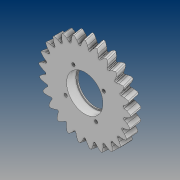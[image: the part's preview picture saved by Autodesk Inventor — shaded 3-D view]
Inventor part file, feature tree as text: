
AUTODESK INVENTOR PART (.ipt)
format: ipt  version: 2021 (Build 250183000, 183)  size: 912,896 bytes
history: native  units: in
note: dims shown in document units (in); Inventor stores cm internally (conversion verified against a paired STEP export)
features: thread x4, sketch x4, extrude x3, pattern_circular x2, plane x1, revolve x1
ambient origin geometry x8: Origin, YZ Plane, XZ Plane, XY Plane, X Axis, Y Axis, Z Axis, Center Point
bodies: Solid2 (feature_tree), Solid1 (feature_tree)
feature tree (15):
  extrude  "Extrusion1"  Depth=0.9055in TaperAngle=0.0deg
  extrude  "Extrusion2"  TaperAngle=0.0deg  [1 undecoded]
  extrude  "Extrusion3"  Depth=0.5118in TaperAngle=0.0deg
  pattern_circular  "Circular Pattern1"  Count=4 Angle=360.0deg
  thread  "Thread1"  [1 undecoded]
  thread  "Thread2"  [1 undecoded]
  thread  "Thread3"  [1 undecoded]
  thread  "Thread4"  [1 undecoded]
  plane  "Work Plane1"
  revolve  "Revolution1"  Angle=90.0deg
  pattern_circular  "Circular Pattern2"  Count=4 Angle=360.0deg
  sketch  "Sketch1"  dims[d0=3.5433in d1=0.9055in d2=0.0in]
  sketch  "Sketch2"  dims[d4=3.3071in d5=0.0in d6=0.0in]
  sketch  "Sketch3"  dims[d8=0.315in d9=0.5118in d10=0.0in d11=1.5748in d12=360.0deg d14=0.3937in d15=0.0in d16=0.3937in d17=0.0in d18=0.3937in d19=0.0in d20=0.3937in d21=0.0in]
  sketch  "Sketch4"  dims[d22=1.125in d23=90.0deg d24=1.5748in d25=360.0deg]
note: 5 required parameter values undecoded (feature->parameter linkage not recoverable at this tier; creation-order binding heuristic only, values carry confidence <= 0.55)
